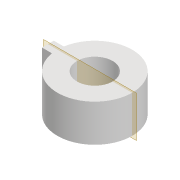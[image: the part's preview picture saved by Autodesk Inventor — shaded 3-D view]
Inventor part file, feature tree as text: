
AUTODESK INVENTOR PART (.ipt)
format: ipt  version: 2022 (Build 260153000, 153)  size: 92,672 bytes
history: native  units: mm
features: extrude x1, sketch x1
ambient origin geometry x8: Origin, YZ Plane, XZ Plane, XY Plane, X Axis, Y Axis, Z Axis, Center Point
bodies: Solid1 (feature_tree)
feature tree (2):
  extrude  "Extrusion1"  Depth=10.0mm
  sketch  "Sketch1"  dims[d0=20.0mm d1=9.534878mm d2=10.0mm d3=0.0mm]
